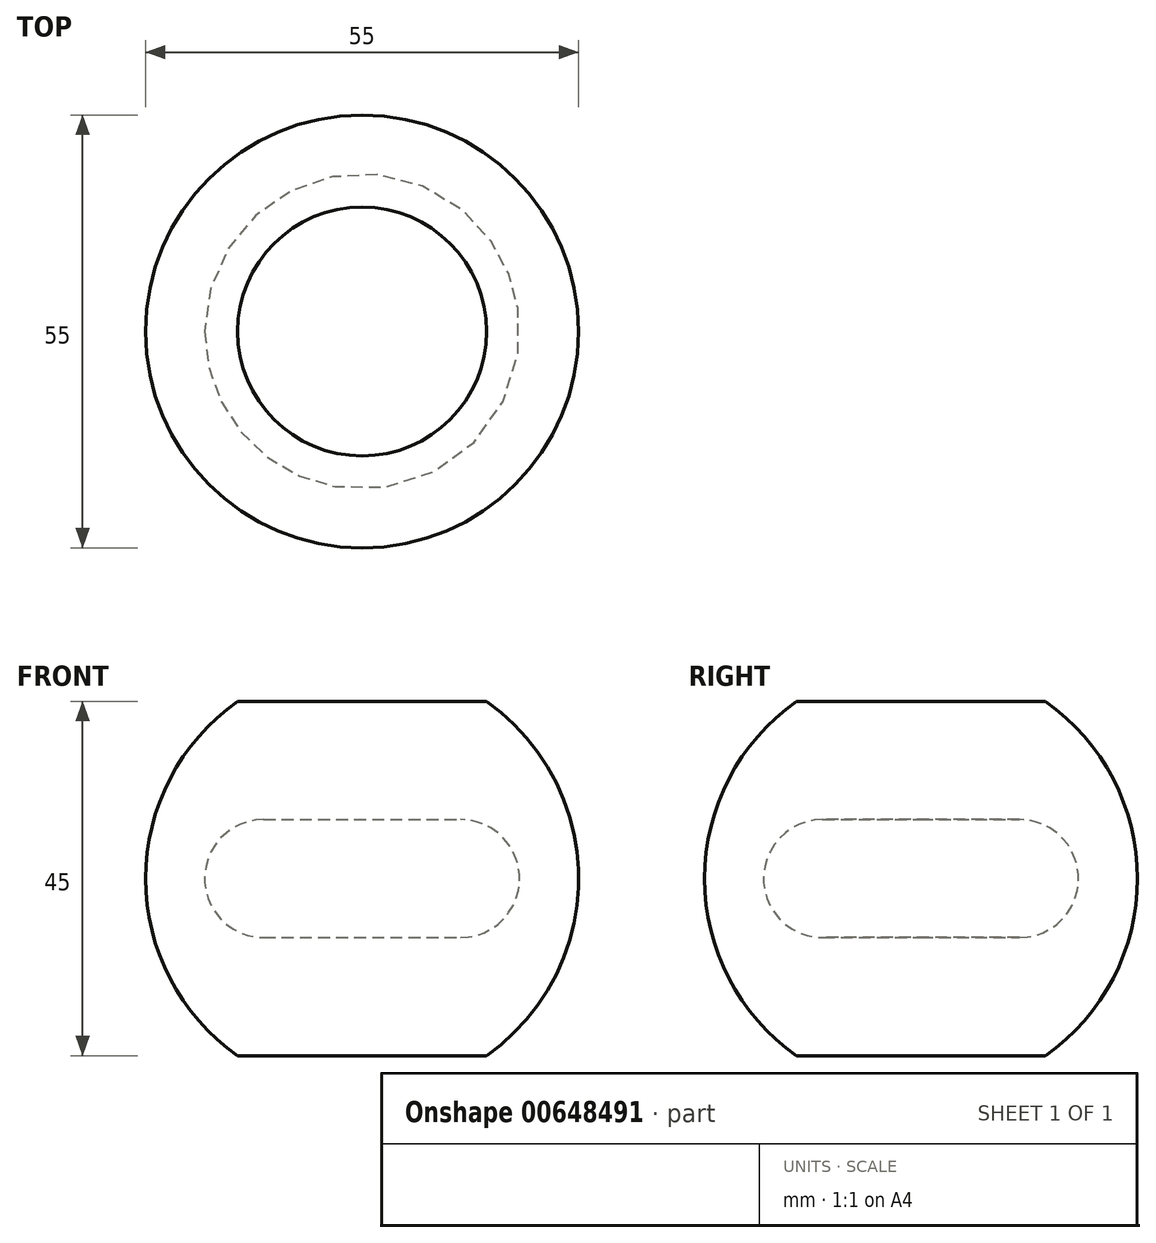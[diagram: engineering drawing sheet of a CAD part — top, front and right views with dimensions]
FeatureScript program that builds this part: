
annotation { "Feature Type Name" : "Feature", "Feature Type Description" : "" }
export const myFeature = defineFeature(function(context is Context, id is Id, definition is map)
    precondition{}
    {
        {
            var Q0;
            Q0=qCreatedBy(makeId("Front.planeOp"),FACE);
            var sketch = newSketch(context, id + "F0", { "sketchPlane" : qUnion([Q0])});
            skLineSegment(sketch, "E0", {"start": v(0, 34.43) * mm, "end": v(0, -32.51) * mm});
            skCircle(sketch, "E1", {"center": v(0, 0) * mm, "radius": 27.5 * mm});
            skLineSegment(sketch, "E2", {"start": v(-15.81, 22.5) * mm, "end": v(15.81, 22.5) * mm});
            skLineSegment(sketch, "E3", {"start": v(-15.81, -22.5) * mm, "end": v(15.81, -22.5) * mm});
            skSolve(sketch);
        }
        {
            var Q0;
            {var subQ0=sQuery(id+"F0.wireOp",EDGE,"E2");var subQ1=sQuery(id+"F0.wireOp",EDGE,"E0");var subQ2=makeQuery(id+"F0.imprint","INTERSECT",VERTEX,{"derivedFrom":[subQ1,subQ0]});Q0=makeQuery(id+"F0.imprint","IMPRINT",FACE,{"disambiguationData":[TD([[makeQuery(id+"F0.imprint","IMPRINT",EDGE,{"disambiguationData":[TD([[subQ2,-1.0]])],"derivedFrom":subQ1}),1.0]])]});}
            var Q1;
            Q1=sQuery(id+"F0.wireOp",EDGE,"E0");
            revolve(context, id + "F1", {"entities" : qUnion([Q0]), "axis" : qUnion([Q1]), "revolveType" : RevolveType.FULL});
        }
        {
            var Q0;
            Q0=qCreatedBy(makeId("Front.planeOp"),FACE);
            var sketch = newSketch(context, id + "F2", { "sketchPlane" : qUnion([Q0])});
            skLineSegment(sketch, "E4.bottom", {"start": v(-12.5, 7.5) * mm, "end": v(12.5, 7.5) * mm});
            skLineSegment(sketch, "E4.top", {"start": v(-12.5, -7.5) * mm, "end": v(12.5, -7.5) * mm});
            skLineSegment(sketch, "E4.left", {"start": v(-20, 0) * mm, "end": v(-20, 0) * mm});
            skLineSegment(sketch, "E4.right", {"start": v(20, 0) * mm, "end": v(20, 0) * mm});
            skLineSegment(sketch, "E5", {"start": v(0, 31.03) * mm, "end": v(0, -38.34) * mm, "construction": true});
            skLineSegment(sketch, "E6", {"start": v(-32.67, 0) * mm, "end": v(38.18, 0) * mm, "construction": true});
            skPoint(sketch, "E7.visualSharp", {"position": v(-20, 7.5) * mm});
            skArc(sketch, "E7.filletArc", {"start": v(-12.5, 7.5) * mm, "mid": v(-17.8, 5.3) * mm, "end": v(-20, 0) * mm});
            skPoint(sketch, "E8.visualSharp", {"position": v(20, 7.5) * mm});
            skArc(sketch, "E8.filletArc", {"start": v(20, 0) * mm, "mid": v(17.8, 5.3) * mm, "end": v(12.5, 7.5) * mm});
            skPoint(sketch, "E9.visualSharp", {"position": v(-20, -7.5) * mm});
            skArc(sketch, "E9.filletArc", {"start": v(-20, 0) * mm, "mid": v(-17.8, -5.3) * mm, "end": v(-12.5, -7.5) * mm});
            skPoint(sketch, "E10.visualSharp", {"position": v(20, -7.5) * mm});
            skArc(sketch, "E10.filletArc", {"start": v(12.5, -7.5) * mm, "mid": v(17.8, -5.3) * mm, "end": v(20, 0) * mm});
            skLineSegment(sketch, "E11", {"start": v(0, 7.5) * mm, "end": v(0, -7.5) * mm});
            skSolve(sketch);
        }
        {
            var Q0;
            {var subQ1=sQuery(id+"F2.wireOp",EDGE,"E8.filletArc");Q0=makeQuery(id+"F2.imprint","IMPRINT",FACE,{"disambiguationData":[TD([[makeQuery(id+"F2.imprint","IMPRINT",EDGE,{"derivedFrom":subQ1}),1.0]])]});}
            var Q1;
            Q1=sQuery(id+"F2.wireOp",EDGE,"E5");
            revolve(context, id + "F3", {"operationType" : NewBodyOperationType.REMOVE, "entities" : qUnion([Q0]), "axis" : qUnion([Q1]), "revolveType" : RevolveType.FULL, "oppositeDirection" : true});
        }
    });
